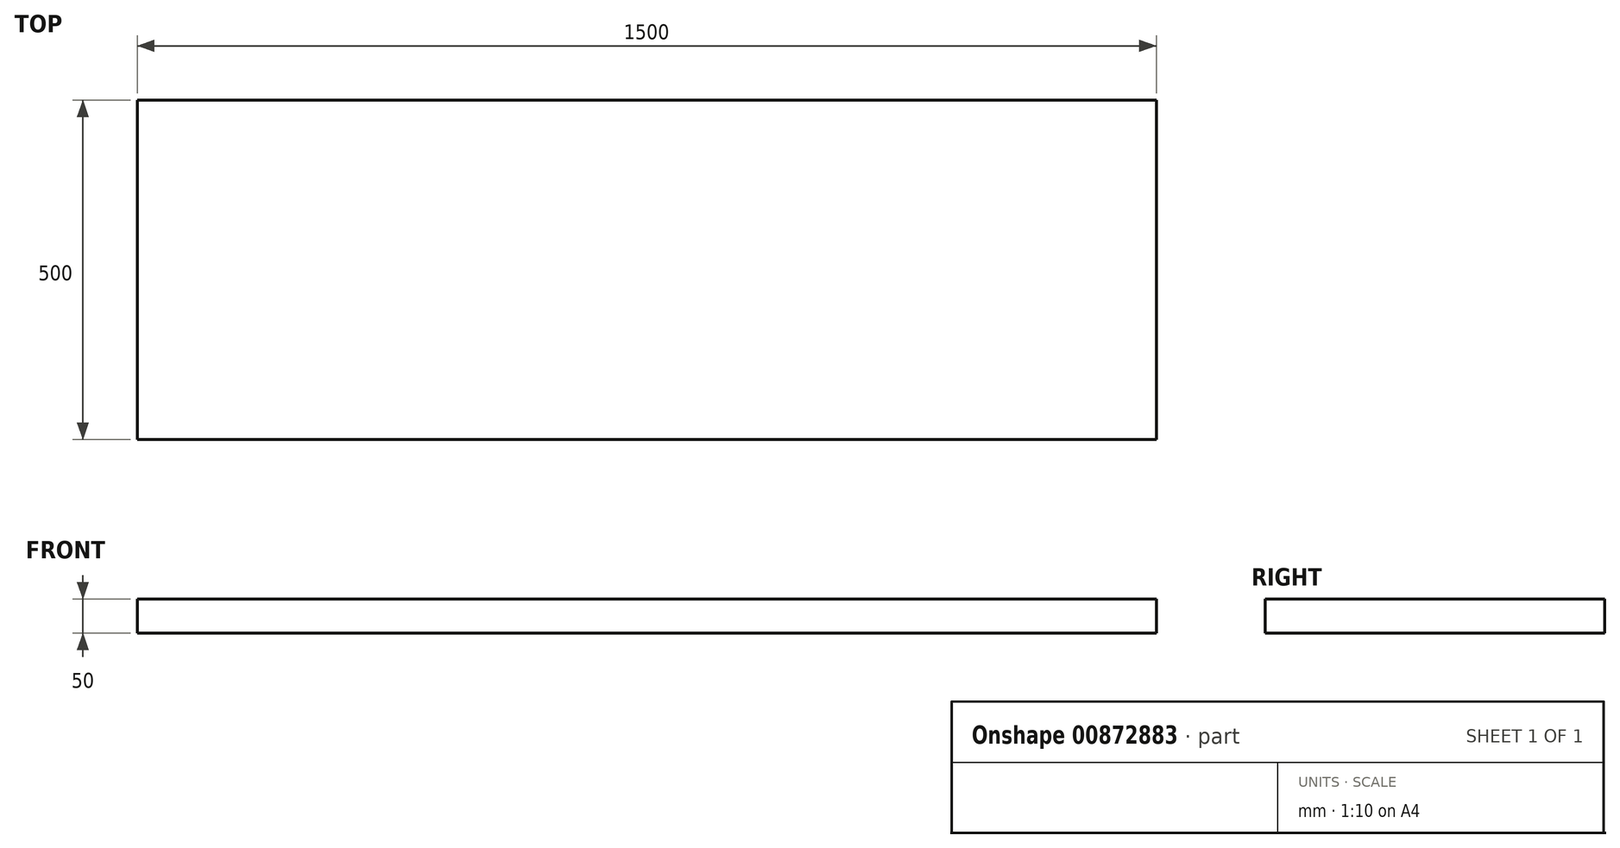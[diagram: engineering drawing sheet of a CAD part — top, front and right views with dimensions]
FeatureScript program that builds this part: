
annotation { "Feature Type Name" : "Feature", "Feature Type Description" : "" }
export const myFeature = defineFeature(function(context is Context, id is Id, definition is map)
    precondition{}
    {
        {
            var Q0;
            Q0=qCreatedBy(makeId("Top.planeOp"),FACE);
            var sketch = newSketch(context, id + "F0", { "sketchPlane" : qUnion([Q0])});
            skLineSegment(sketch, "E0.bottom", {"start": v(0, 0) * mm, "end": v(1500, 0) * mm});
            skLineSegment(sketch, "E0.top", {"start": v(0, -500) * mm, "end": v(1500, -500) * mm});
            skLineSegment(sketch, "E0.left", {"start": v(0, 0) * mm, "end": v(0, -500) * mm});
            skLineSegment(sketch, "E0.right", {"start": v(1500, 0) * mm, "end": v(1500, -500) * mm});
            skSolve(sketch);
        }
        {
            var Q0;
            Q0=makeQuery(id+"F0.imprint","IMPRINT",FACE,{"disambiguationData":[TD([[makeQuery(id+"F0.imprint","IMPRINT",EDGE,{"derivedFrom":sQuery(id+"F0.wireOp",EDGE,"E0.bottom")}),-1.0]])]});
            extrude(context, id + "F1", {"entities" : qUnion([Q0]), "depth" : 50 * mm, "offsetDistance" : 25 * mm});
        }
    });
